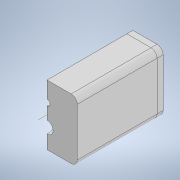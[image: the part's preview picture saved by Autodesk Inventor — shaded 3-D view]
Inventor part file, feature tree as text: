
AUTODESK INVENTOR PART (.ipt)
format: ipt  version: 2022 (Build 260153000, 153)  size: 19,995,136 bytes
history: native  units: mm
features: other x5, move_body x1, extrude x1, chamfer x1, sketch x1, projected_geometry x1
ambient origin geometry x8: Origin, YZ Plane, XZ Plane, XY Plane, X Axis, Y Axis, Z Axis, Center Point
bodies: Solid2 (feature_tree), Solid1 (feature_tree)
feature tree (10):
  other  "Queen Mold.ipt"
  other  "MeshFeature1"
  move_body  "Move Body1"
  extrude  "Extrusion1"  Depth=2.0mm
  chamfer  "Chamfer1"  Distance=4.0mm
  other  "Solid2::Queen Mold.ipt"
  other  "TaggingFeature1"
  other  "Work Axis1"
  sketch  "Sketch1"  dims[d0=10.0mm d1=-100.248mm d2=2516.89mm d3=-1.844134mm d4=4.0mm d5=0.0mm d6=1.0mm d7=2.0mm d8=45.0deg]
  projected_geometry  "Projected Loop1"
